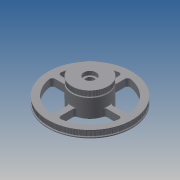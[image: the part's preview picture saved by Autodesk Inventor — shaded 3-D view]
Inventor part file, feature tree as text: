
AUTODESK INVENTOR PART (.ipt)
format: ipt  version: 2013 (Build 170138000, 138)  size: 4,050,432 bytes
history: native  units: mm
features: extrude x5, sketch x5, other x3, fillet x1, pattern_circular x1, projected_geometry x1
ambient origin geometry x8: Origin, YZ Plane, XZ Plane, XY Plane, X Axis, Y Axis, Z Axis, Center Point
bodies: Solid1 (feature_tree)
feature tree (16):
  other  "distal idler pulley.iam"
  other  "235 pulley blank.ipt:1"
  other  "100 pulley blank.ipt:1"
  extrude  "Extrusion1"  Depth=10.0mm TaperAngle=0.0deg
  extrude  "Extrusion2"  Depth=5.0mm
  fillet  "Fillet1"  [1 undecoded]
  pattern_circular  "Circular Pattern1"  Count=4 Angle=360.0deg
  extrude  "Extrusion3"  Depth=15.0mm
  extrude  "Extrusion4"  Depth=10.0mm TaperAngle=0.0deg
  extrude  "Extrusion5"  Depth=22.0mm
  sketch  "Sketch1"  dims[d0=10.0mm d1=10.0mm d2=0.0mm]
  projected_geometry  "Projected Loop1"
  sketch  "Sketch2"  dims[d3=5.0mm d4=5.0mm d5=0.0mm]
  sketch  "Sketch3"  dims[d6=12.0mm]
  sketch  "Sketch4"  dims[d7=10.0mm d8=0.0mm]
  sketch  "Sketch5"  dims[d9=5.0mm d10=40.0mm d11=360.0deg d13=15.0mm d15=10.0mm d16=0.0mm d17=22.0mm d19=7.0mm d20=0.0mm d21=22.0mm d23=7.0mm d24=0.0mm]
note: 1 required parameter value undecoded (feature->parameter linkage not recoverable at this tier; creation-order binding heuristic only, values carry confidence <= 0.55)
